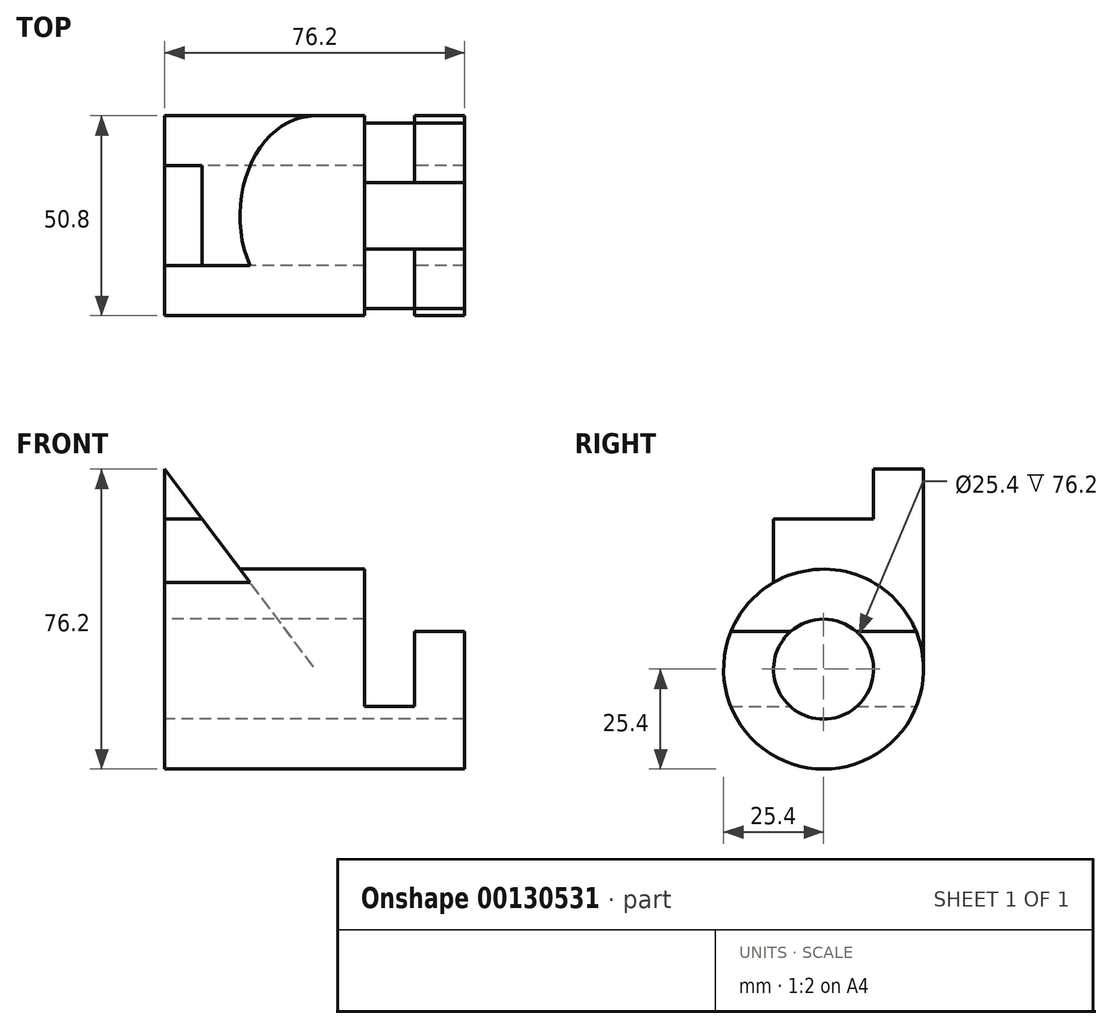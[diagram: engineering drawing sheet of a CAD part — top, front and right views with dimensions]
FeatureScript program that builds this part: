
annotation { "Feature Type Name" : "Feature", "Feature Type Description" : "" }
export const myFeature = defineFeature(function(context is Context, id is Id, definition is map)
    precondition{}
    {
        {
            var Q0;
            Q0=qCreatedBy(makeId("Right.planeOp"),FACE);
            var sketch = newSketch(context, id + "F0", { "sketchPlane" : qUnion([Q0])});
            skCircle(sketch, "E0", {"center": v(0, 0) * mm, "radius": 12.7 * mm});
            skCircle(sketch, "E1", {"center": v(0, 0) * mm, "radius": 25.4 * mm});
            skSolve(sketch);
        }
        {
            var Q0;
            Q0 = qSketchRegion(id + "F0", true);
            extrude(context, id + "F1", {"entities" : qUnion([Q0]), "depth" : 50.8 * mm});
        }
        {
            var Q0;
            Q0=makeQuery(id+"F1.opExtrude","CAP_FACE",FACE,{"disambiguationData":[OSD([sQuery(id+"F0.wireOp",EDGE,"E0"),sQuery(id+"F0.wireOp",EDGE,"E1")])],"isStart":false});
            var sketch = newSketch(context, id + "F2", { "sketchPlane" : qUnion([Q0])});
            skCircle(sketch, "E2.0", {"center": v(0, 0) * mm, "radius": 25.4 * mm});
            skCircle(sketch, "E2.1", {"center": v(0, 0) * mm, "radius": 12.7 * mm});
            skLineSegment(sketch, "E3", {"start": v(-23.55, -9.52) * mm, "end": v(-8.4, -9.52) * mm});
            skLineSegment(sketch, "E4", {"start": v(8.4, -9.52) * mm, "end": v(23.55, -9.52) * mm});
            skPoint(sketch, "E5", {"position": v(0, 25.4) * mm});
            skSolve(sketch);
        }
        {
            var Q0;
            {var subQ0=sQuery(id+"F2.wireOp",EDGE,"E3");Q0=makeQuery(id+"F2.imprint","IMPRINT",FACE,{"disambiguationData":[TD([[makeQuery(id+"F2.imprint","IMPRINT",EDGE,{"derivedFrom":subQ0}),-1.0]])]});}
            extrude(context, id + "F3", {"entities" : qUnion([Q0]), "operationType" : NewBodyOperationType.ADD, "depth" : 12.7 * mm});
        }
        {
            var Q0;
            Q0=makeQuery(id+"F3.opExtrude","CAP_FACE",FACE,{"disambiguationData":[OSD([sQuery(id+"F2.wireOp",EDGE,"E2.0"),sQuery(id+"F2.wireOp",EDGE,"E2.1"),sQuery(id+"F2.wireOp",EDGE,"E3"),sQuery(id+"F2.wireOp",EDGE,"E4")])],"isStart":false});
            var sketch = newSketch(context, id + "F4", { "sketchPlane" : qUnion([Q0])});
            skArc(sketch, "E6.0", {"start": v(23.55, -9.52) * mm, "mid": v(0, 25.4) * mm, "end": v(-23.55, -9.52) * mm});
            skArc(sketch, "E6.1", {"start": v(8.4, -9.52) * mm, "mid": v(0, 12.7) * mm, "end": v(-8.4, -9.52) * mm});
            skArc(sketch, "E7.0", {"start": v(-23.55, -9.52) * mm, "mid": v(0, -25.4) * mm, "end": v(23.55, -9.53) * mm});
            skArc(sketch, "E7.1", {"start": v(-8.4, -9.52) * mm, "mid": v(0, -12.7) * mm, "end": v(8.4, -9.52) * mm});
            skLineSegment(sketch, "E8", {"start": v(-23.55, 9.53) * mm, "end": v(-8.4, 9.53) * mm});
            skLineSegment(sketch, "E9", {"start": v(8.4, 9.53) * mm, "end": v(23.55, 9.53) * mm});
            skPoint(sketch, "E10", {"position": v(0, 25.4) * mm});
            skSolve(sketch);
        }
        {
            var Q0;
            {var subQ2=sQuery(id+"F4.wireOp",EDGE,"E8");Q0=makeQuery(id+"F4.imprint","IMPRINT",FACE,{"disambiguationData":[TD([[makeQuery(id+"F4.imprint","IMPRINT",EDGE,{"derivedFrom":subQ2}),-1.0]])]});}
            var Q1;
            {var subQ2=sQuery(id+"F4.wireOp",EDGE,"E9");Q1=makeQuery(id+"F4.imprint","IMPRINT",FACE,{"disambiguationData":[TD([[makeQuery(id+"F4.imprint","IMPRINT",EDGE,{"derivedFrom":subQ2}),-1.0]])]});}
            var Q2;
            Q2=makeQuery(id+"F4.imprint","IMPRINT",FACE,{"disambiguationData":[TD([[makeQuery(id+"F4.imprint","IMPRINT",EDGE,{"derivedFrom":sQuery(id+"F4.wireOp",EDGE,"E7.0")}),1.0]])]});
            extrude(context, id + "F5", {"entities" : qUnion([Q0, Q1, Q2]), "operationType" : NewBodyOperationType.ADD, "depth" : 12.7 * mm});
        }
        {
            var Q0;
            Q0=qCreatedBy(makeId("Front.planeOp"),FACE);
            cPlane(context, id + "F6", {"entities" : qUnion([Q0]), "cplaneType" : CPlaneType.OFFSET, "offset" : 12.7 * mm, "width" : 152.4 * mm, "height" : 152.4 * mm});
        }
        {
            var Q0;
            Q0=qCreatedBy(id+"F6.planeOp",FACE);
            var sketch = newSketch(context, id + "F7", { "sketchPlane" : qUnion([Q0])});
            skLineSegment(sketch, "E11.0", {"start": v(0, 25.4) * mm, "end": v(0, -25.4) * mm});
            skLineSegment(sketch, "E12", {"start": v(0, 25.4) * mm, "end": v(0, 38.1) * mm});
            skLineSegment(sketch, "E13", {"start": v(0, 38.1) * mm, "end": v(0, 50.8) * mm});
            skLineSegment(sketch, "E14", {"start": v(0, 0) * mm, "end": v(76.2, 0) * mm, "construction": true});
            skPoint(sketch, "E15", {"position": v(38.1, 0) * mm});
            skLineSegment(sketch, "E16", {"start": v(0, 50.8) * mm, "end": v(38.1, 0) * mm});
            skLineSegment(sketch, "E17.0", {"start": v(50.8, -9.53) * mm, "end": v(50.8, 25.4) * mm});
            skLineSegment(sketch, "E18", {"start": v(0, 25.4) * mm, "end": v(50.8, 25.4) * mm, "construction": true});
            skPoint(sketch, "E19", {"position": v(19.05, 25.4) * mm});
            skLineSegment(sketch, "E20", {"start": v(0, 25.4) * mm, "end": v(19.05, 25.4) * mm});
            skLineSegment(sketch, "E21", {"start": v(0, 38.1) * mm, "end": v(9.53, 38.1) * mm});
            skLineSegment(sketch, "E22", {"start": v(0, 25.4) * mm, "end": v(0, 19.05) * mm});
            skLineSegment(sketch, "E23", {"start": v(0, 19.05) * mm, "end": v(23.81, 19.05) * mm});
            skSolve(sketch);
        }
        {
            var Q0;
            {var subQ0=sQuery(id+"F7.wireOp",EDGE,"E20");Q0=makeQuery(id+"F7.imprint","IMPRINT",FACE,{"disambiguationData":[TD([[makeQuery(id+"F7.imprint","IMPRINT",EDGE,{"derivedFrom":subQ0}),-1.0]])]});}
            var Q1;
            Q1=makeQuery(id+"F7.imprint","IMPRINT",FACE,{"disambiguationData":[TD([[makeQuery(id+"F7.imprint","IMPRINT",EDGE,{"derivedFrom":sQuery(id+"F7.wireOp",EDGE,"E12")}),-1.0]])]});
            extrude(context, id + "F8", {"entities" : qUnion([Q0, Q1]), "operationType" : NewBodyOperationType.ADD, "oppositeDirection" : true, "depth" : 25.4 * mm});
        }
        {
            var Q0;
            Q0=makeQuery(id+"F8.opExtrude","CAP_FACE",FACE,{"disambiguationData":[OSD([sQuery(id+"F7.wireOp",EDGE,"E12"),sQuery(id+"F7.wireOp",EDGE,"E16"),sQuery(id+"F7.wireOp",EDGE,"E21"),sQuery(id+"F7.wireOp",EDGE,"E22"),sQuery(id+"F7.wireOp",EDGE,"E23")])],"isStart":false});
            var sketch = newSketch(context, id + "F9", { "sketchPlane" : qUnion([Q0])});
            skLineSegment(sketch, "E24.0", {"start": v(0, 38.1) * mm, "end": v(-9.53, 38.1) * mm});
            skLineSegment(sketch, "E24.1", {"start": v(0, 38.1) * mm, "end": v(0, 50.8) * mm});
            skLineSegment(sketch, "E24.2", {"start": v(0, 25.4) * mm, "end": v(0, 38.1) * mm});
            skLineSegment(sketch, "E25", {"start": v(0, 25.4) * mm, "end": v(0, 0) * mm});
            skLineSegment(sketch, "E26", {"start": v(0, 50.8) * mm, "end": v(-38.1, 0) * mm});
            skLineSegment(sketch, "E27", {"start": v(-38.1, 0) * mm, "end": v(0, 0) * mm});
            skSolve(sketch);
        }
        {
            var Q0;
            Q0 = qSketchRegion(id + "F9", true);
            extrude(context, id + "F10", {"entities" : qUnion([Q0]), "operationType" : NewBodyOperationType.ADD, "depth" : 12.7 * mm});
        }
    });
